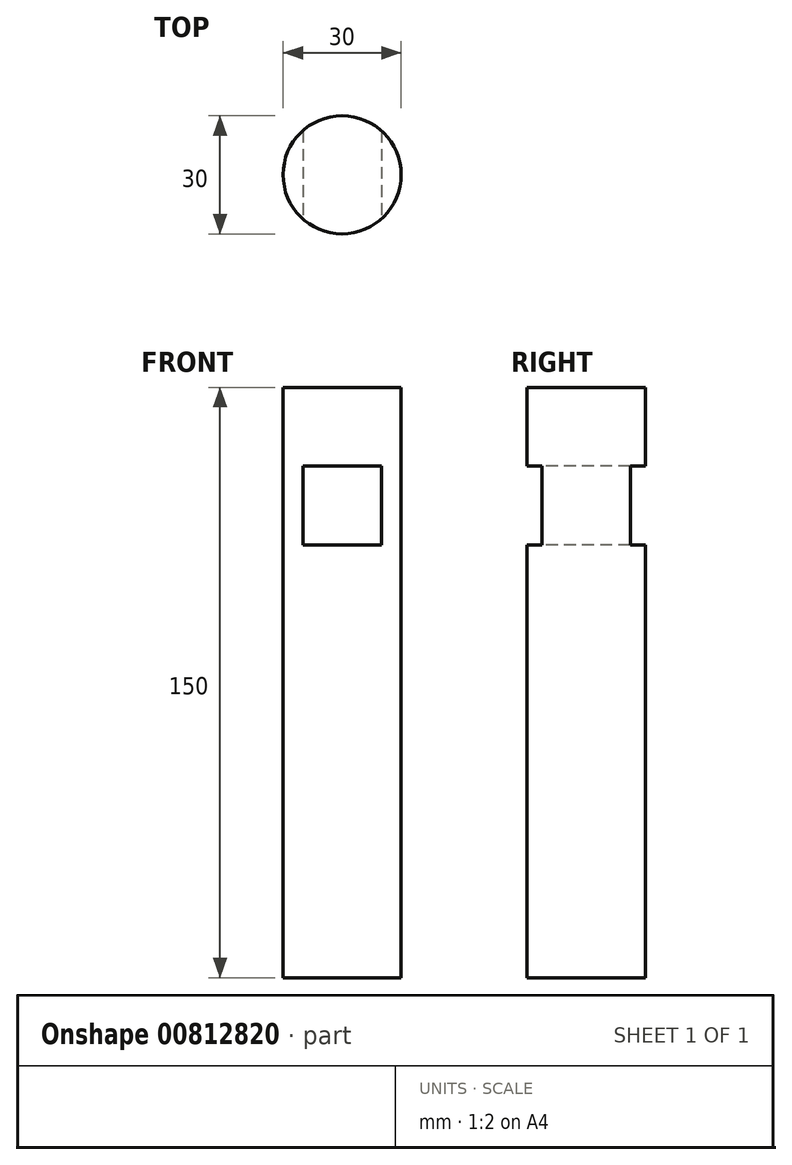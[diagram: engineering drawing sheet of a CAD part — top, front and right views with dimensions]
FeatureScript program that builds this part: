
annotation { "Feature Type Name" : "Feature", "Feature Type Description" : "" }
export const myFeature = defineFeature(function(context is Context, id is Id, definition is map)
    precondition{}
    {
        {
            var Q0;
            Q0=qCreatedBy(makeId("Top.planeOp"),FACE);
            var sketch = newSketch(context, id + "F0", { "sketchPlane" : qUnion([Q0])});
            skCircle(sketch, "E0", {"center": v(0, 0) * mm, "radius": 15 * mm});
            skSolve(sketch);
        }
        {
            var Q0;
            Q0 = qSketchRegion(id + "F0", true);
            extrude(context, id + "F1", {"entities" : qUnion([Q0]), "depth" : 150 * mm, "offsetDistance" : 25 * mm});
        }
        {
            var Q0;
            Q0=qCreatedBy(makeId("Front.planeOp"),FACE);
            var sketch = newSketch(context, id + "F2", { "sketchPlane" : qUnion([Q0])});
            skLineSegment(sketch, "E1.bottom", {"start": v(-10, 130) * mm, "end": v(10, 130) * mm});
            skLineSegment(sketch, "E1.top", {"start": v(-10, 110) * mm, "end": v(10, 110) * mm});
            skLineSegment(sketch, "E1.left", {"start": v(-10, 130) * mm, "end": v(-10, 110) * mm});
            skLineSegment(sketch, "E1.right", {"start": v(10, 130) * mm, "end": v(10, 110) * mm});
            skSolve(sketch);
        }
        {
            var Q0;
            Q0 = qSketchRegion(id + "F2", true);
            extrude(context, id + "F3", {"entities" : qUnion([Q0]), "operationType" : NewBodyOperationType.REMOVE, "endBound" : BoundingType.SYMMETRIC, "oppositeDirection" : true, "depth" : 50 * mm, "offsetDistance" : 25 * mm});
        }
    });
